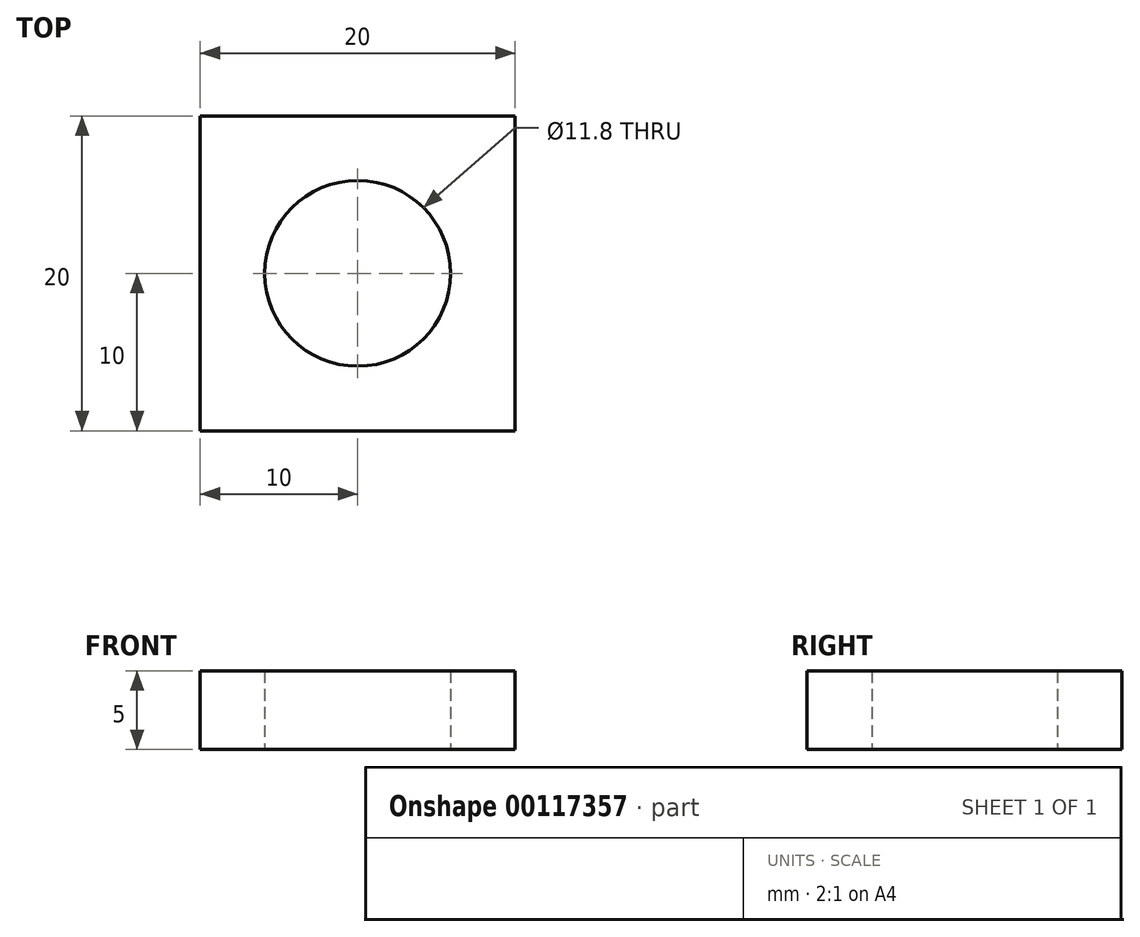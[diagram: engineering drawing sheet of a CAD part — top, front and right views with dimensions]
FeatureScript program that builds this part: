
annotation { "Feature Type Name" : "Feature", "Feature Type Description" : "" }
export const myFeature = defineFeature(function(context is Context, id is Id, definition is map)
    precondition{}
    {
        {
            var Q0;
            Q0=qCreatedBy(makeId("Top.planeOp"),FACE);
            var sketch = newSketch(context, id + "F0", { "sketchPlane" : qUnion([Q0])});
            skLineSegment(sketch, "E0.bottom", {"start": v(10, 10) * mm, "end": v(-10, 10) * mm});
            skLineSegment(sketch, "E0.top", {"start": v(10, -10) * mm, "end": v(-10, -10) * mm});
            skLineSegment(sketch, "E0.left", {"start": v(10, 10) * mm, "end": v(10, -10) * mm});
            skLineSegment(sketch, "E0.right", {"start": v(-10, 10) * mm, "end": v(-10, -10) * mm});
            skPoint(sketch, "E0.middle", {"position": v(0, 0) * mm});
            skCircle(sketch, "E1", {"center": v(0, 0) * mm, "radius": 5.9 * mm});
            skSolve(sketch);
        }
        {
            var Q0;
            Q0 = qSketchRegion(id + "F0", true);
            extrude(context, id + "F1", {"entities" : qUnion([Q0]), "depth" : 5 * mm});
        }
    });
